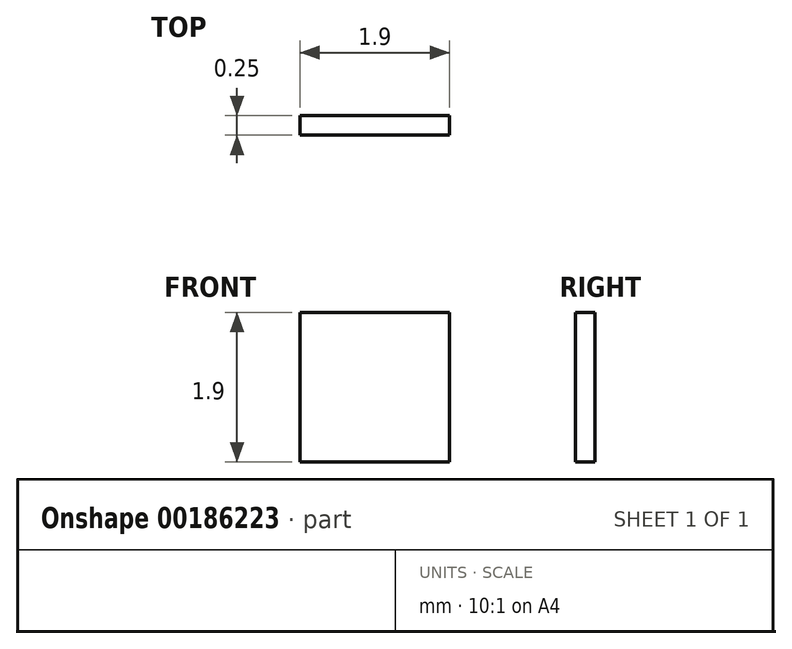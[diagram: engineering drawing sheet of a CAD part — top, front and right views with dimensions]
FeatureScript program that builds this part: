
annotation { "Feature Type Name" : "Feature", "Feature Type Description" : "" }
export const myFeature = defineFeature(function(context is Context, id is Id, definition is map)
    precondition{}
    {
        {
            var Q0;
            Q0=qCreatedBy(makeId("Front.planeOp"),FACE);
            var sketch = newSketch(context, id + "F0", { "sketchPlane" : qUnion([Q0])});
            skLineSegment(sketch, "E0.bottom", {"start": v(0.95, 0.95) * mm, "end": v(-0.95, 0.95) * mm});
            skLineSegment(sketch, "E0.top", {"start": v(0.95, -0.95) * mm, "end": v(-0.95, -0.95) * mm});
            skLineSegment(sketch, "E0.left", {"start": v(0.95, 0.95) * mm, "end": v(0.95, -0.95) * mm});
            skLineSegment(sketch, "E0.right", {"start": v(-0.95, 0.95) * mm, "end": v(-0.95, -0.95) * mm});
            skPoint(sketch, "E0.middle", {"position": v(0, 0) * mm});
            skSolve(sketch);
        }
        {
            var Q0;
            Q0=makeQuery(id+"F0.imprint","IMPRINT",FACE,{"disambiguationData":[TD([[makeQuery(id+"F0.imprint","IMPRINT",EDGE,{"derivedFrom":sQuery(id+"F0.wireOp",EDGE,"E0.bottom")}),1.0]])]});
            extrude(context, id + "F1", {"entities" : qUnion([Q0]), "depth" : 0.25 * mm});
        }
    });
